# Revit family: Joist_NewMillennium_K-Series_BowString
name_source: partatom
category: Structural Framing
units: mm (PartAtom-declared; Revit-internal decimal feet)

## family parameters
Always export as geometry = No
Always vertical = Yes
Classification Number = 23.25.30.21.14.11
Cut with Voids When Loaded = No
Material for Model Behavior = Steel
Section Shape = Not Defined
Shared = No
Show family pre-cut in plan views = Yes

## types (11) — shared parameters
Assembly Code = B1010350
Bearing Seat = Yes
Bottom Chord Offset from End = 3' - 0"
Building Codes = https://www.newmill.com
Channel Width = 0' - 1 1/8"
Construction Details = https://www.newmill.com
Description = New Millennium Building Systems K Series - Bowstring
Green Building-LEED = http://www.arcat.com
Installation-Fabrication = https://www.newmill.com
Keynote = 05 21 00
Lower Chord Representation = Metal - Steel
Manufacturer = New Millennium Building Systems
Manufacturer Fax = 260-868-6002
Manufacturer Website = https://www.newmill.com
Maximum Length = 20' - 0"
Model = K Series - Bowstring
Product Data = http://www.arcat.com
Revision = R0_10-2017
Sales Information = https://www.newmill.com
Seat Length = 0' - 9"
Specification = http://www.arcat.com
TXTLoc = 1' - 0 1/2"
Test Data = https://www.newmill.com
Thickness_Channel = 0' - 0 3/16"
Type Comments = Contact New Millennium for Structural Web Design
URL = https://www.newmill.com
Upper Chord Representation = Metal - Steel
Web Infill = Metal - Steel

## per-type parameters (varying)
| type | Angle Size_Lower | Angle Size_Upper | Height | Max Length | Roundover | SeatHalf | SeatWdth | Thickness_Lower | Thickness_Upper |
| 10 in Depth / 20 Ft Max Length | 0' - 1 1/4" | 0' - 1 1/2" | 0' - 10" | 20' - 0" | 0' - 0 1/16" | 0' - 2 1/16" | 0' - 1 3/8" | 0' - 0 3/32" | 0' - 0 1/8" |
| 12 in Depth / 24 Ft Max Length | 0' - 1 1/4" | 0' - 1 1/2" | 1' - 0" | 24' - 0" | 0' - 0 1/16" | 0' - 2 1/16" | 0' - 1 3/8" | 0' - 0 3/32" | 0' - 0 1/8" |
| 14 in Depth / 28 Ft Max Length | 0' - 1 1/4" | 0' - 1 1/2" | 1' - 2" | 28' - 0" | 0' - 0 1/16" | 0' - 2 1/16" | 0' - 1 3/8" | 0' - 0 3/32" | 0' - 0 1/8" |
| 16 in Depth / 32 Ft Max Length | 0' - 1 1/4" | 0' - 1 1/2" | 1' - 4" | 32' - 0" | 0' - 0 1/16" | 0' - 2 1/16" | 0' - 1 3/8" | 0' - 0 3/32" | 0' - 0 1/8" |
| 18 in Depth / 36 Ft Max Length | 0' - 1 1/2" | 0' - 1 1/2" | 1' - 6" | 36' - 0" | 0' - 0 1/16" | 0' - 2 1/16" | 0' - 1 3/8" | 0' - 0 1/8" | 0' - 0 1/8" |
| 20 in Depth / 40 Ft Max Length | 0' - 1 1/2" | 0' - 1 1/2" | 1' - 8" | 40' - 0" | 0' - 0 1/16" | 0' - 2 1/16" | 0' - 1 3/8" | 0' - 0 1/8" | 0' - 0 1/8" |
| 22 in Depth / 44 Ft Max Length | 0' - 1 1/2" | 0' - 1 1/2" | 1' - 10" | 44' - 0" | 0' - 0 1/16" | 0' - 2 1/16" | 0' - 1 3/8" | 0' - 0 1/8" | 0' - 0 1/8" |
| 24 in Depth / 48 Ft Max Length | 0' - 1 1/2" | 0' - 1 3/4" | 2' - 0" | 48' - 0" | 0' - 0 1/16" | 0' - 2 5/16" | 0' - 1 13/32" | 0' - 0 1/8" | 0' - 0 5/32" |
| 26 in Depth / 52 Ft Max Length | 0' - 1 1/2" | 0' - 1 3/4" | 2' - 2" | 52' - 0" | 0' - 0 1/16" | 0' - 2 5/16" | 0' - 1 13/32" | 0' - 0 1/8" | 0' - 0 5/32" |
| 28 in Depth / 56 Ft Max Length | 0' - 2" | 0' - 2" | 2' - 4" | 56' - 0" | 0' - 0 3/32" | 0' - 2 9/16" | 0' - 1 15/32" | 0' - 0 5/32" | 0' - 0 5/32" |
| 30 in Depth / 60 Ft Max Length | 0' - 2" | 0' - 2" | 2' - 6" | 60' - 0" | 0' - 0 3/32" | 0' - 2 9/16" | 0' - 1 15/32" | 0' - 0 5/32" | 0' - 0 5/32" |

## geometry (parser evidence)
native form markers: Sweep x4
no freeform markers — native parametric forms only
